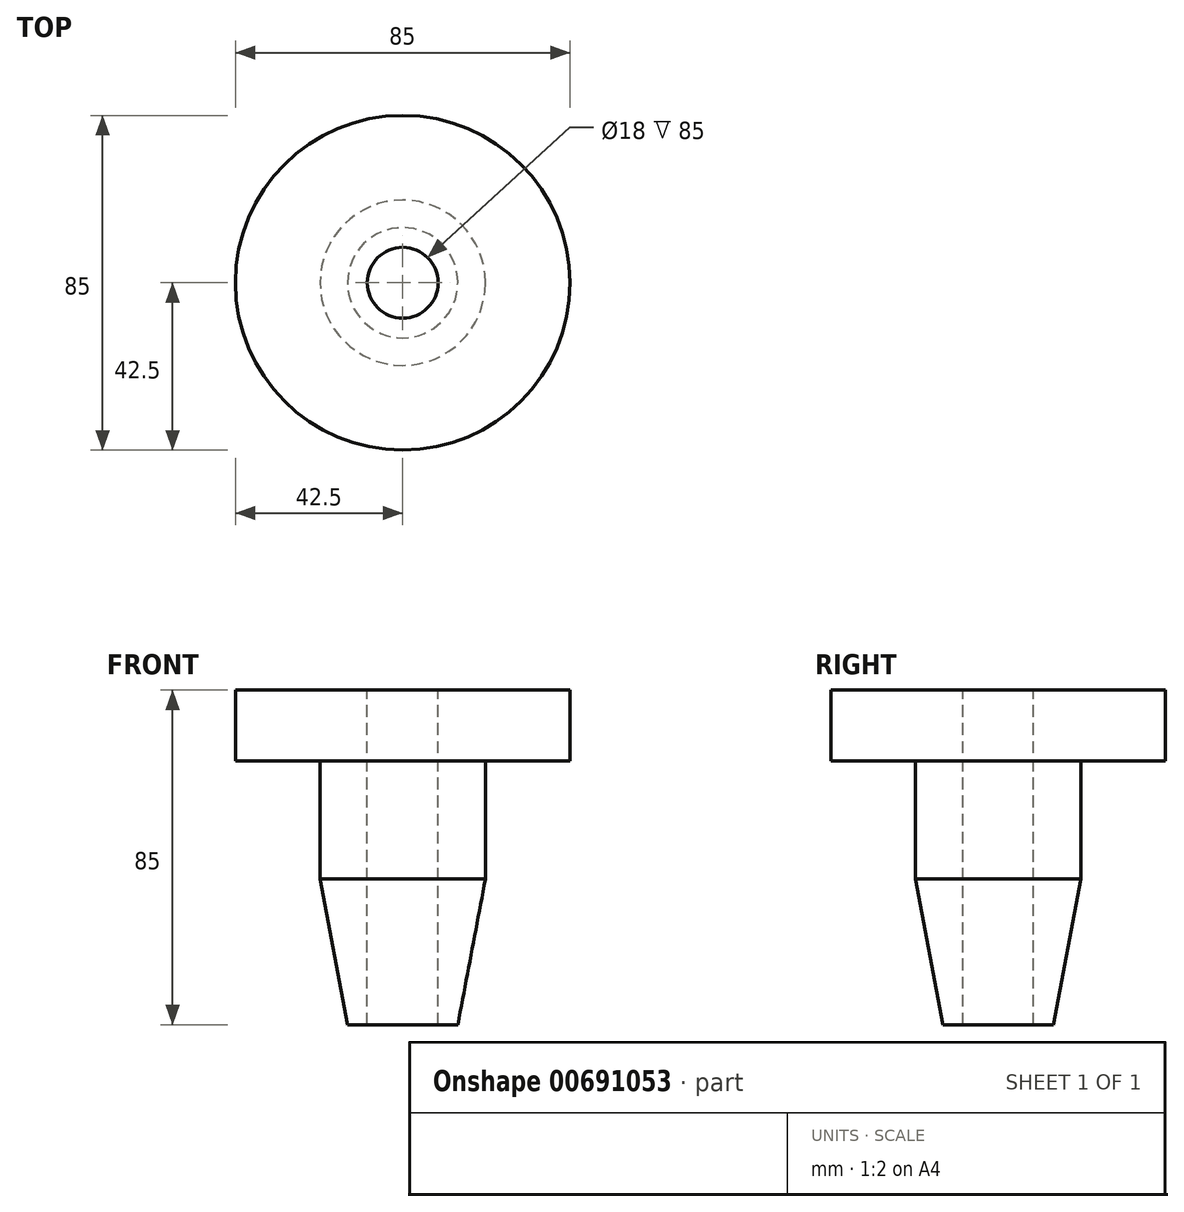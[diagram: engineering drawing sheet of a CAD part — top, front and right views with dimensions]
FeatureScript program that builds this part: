
annotation { "Feature Type Name" : "Feature", "Feature Type Description" : "" }
export const myFeature = defineFeature(function(context is Context, id is Id, definition is map)
    precondition{}
    {
        {
            var Q0;
            Q0=qCreatedBy(makeId("Front.planeOp"),FACE);
            var sketch = newSketch(context, id + "F0", { "sketchPlane" : qUnion([Q0])});
            skLineSegment(sketch, "E0", {"start": v(9, 0) * mm, "end": v(9, -85) * mm});
            skLineSegment(sketch, "E1", {"start": v(21, -48) * mm, "end": v(21, -18) * mm});
            skLineSegment(sketch, "E2", {"start": v(21, -18) * mm, "end": v(42.5, -18) * mm});
            skLineSegment(sketch, "E3", {"start": v(42.5, -18) * mm, "end": v(42.5, 0) * mm});
            skLineSegment(sketch, "E4", {"start": v(42.5, 0) * mm, "end": v(9, 0) * mm});
            skPoint(sketch, "E5.orphan", {"position": v(21, -85) * mm});
            skLineSegment(sketch, "E6", {"start": v(9, -85) * mm, "end": v(14, -85) * mm});
            skLineSegment(sketch, "E7", {"start": v(21, -48) * mm, "end": v(14, -85) * mm});
            skLineSegment(sketch, "E8", {"start": v(0, 0) * mm, "end": v(0, -72.52) * mm});
            skSolve(sketch);
        }
        {
            var Q0;
            Q0=makeQuery(id+"F0.imprint","IMPRINT",FACE,{"disambiguationData":[TD([[makeQuery(id+"F0.imprint","IMPRINT",EDGE,{"derivedFrom":sQuery(id+"F0.wireOp",EDGE,"E0")}),1.0]])]});
            var Q1;
            Q1=sQuery(id+"F0.wireOp",EDGE,"E8");
            revolve(context, id + "F1", {"entities" : qUnion([Q0]), "axis" : qUnion([Q1]), "revolveType" : RevolveType.FULL});
        }
    });
